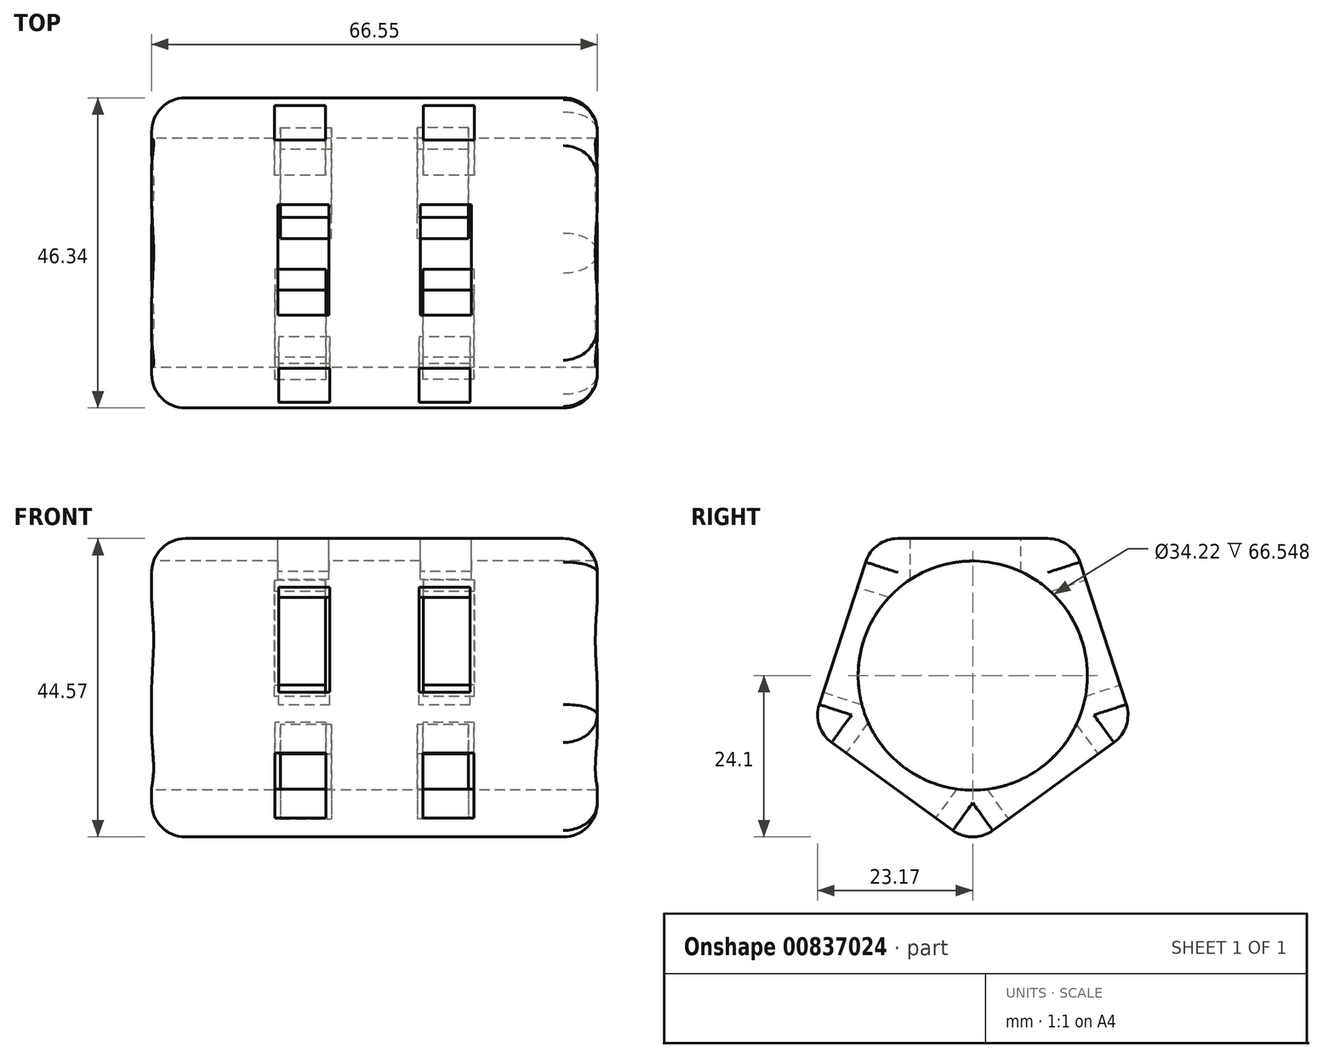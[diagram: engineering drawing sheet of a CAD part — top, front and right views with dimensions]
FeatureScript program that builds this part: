
annotation { "Feature Type Name" : "Feature", "Feature Type Description" : "" }
export const myFeature = defineFeature(function(context is Context, id is Id, definition is map)
    precondition{}
    {
        {
            var Q0;
            Q0=qCreatedBy(makeId("Right.planeOp"),FACE);
            var sketch = newSketch(context, id + "F0", { "sketchPlane" : qUnion([Q0])});
            skCircle(sketch, "E0.cCircle", {"center": v(0, 0) * mm, "radius": 20.47 * mm, "construction": true});
            skLineSegment(sketch, "E0.0", {"start": v(-14.87, 20.47) * mm, "end": v(14.87, 20.47) * mm});
            skLineSegment(sketch, "E0.1", {"start": v(14.87, 20.47) * mm, "end": v(24.07, -7.82) * mm});
            skLineSegment(sketch, "E0.2", {"start": v(24.07, -7.82) * mm, "end": v(0, -25.3) * mm});
            skLineSegment(sketch, "E0.3", {"start": v(0, -25.3) * mm, "end": v(-24.07, -7.82) * mm});
            skLineSegment(sketch, "E0.4", {"start": v(-24.07, -7.82) * mm, "end": v(-14.87, 20.47) * mm});
            skPoint(sketch, "E0.0.midPoint", {"position": v(0, 20.47) * mm});
            skCircle(sketch, "E1", {"center": v(0, 0) * mm, "radius": 17.1 * mm});
            skSolve(sketch);
        }
        {
            var Q0;
            Q0=makeQuery(id+"F0.imprint","IMPRINT",FACE,{"disambiguationData":[TD([[makeQuery(id+"F0.imprint","IMPRINT",EDGE,{"derivedFrom":sQuery(id+"F0.wireOp",EDGE,"E0.0")}),-1.0]])]});
            extrude(context, id + "F1", {"entities" : qUnion([Q0]), "depth" : 66.55 * mm, "offsetDistance" : 25.4 * mm});
        }
        {
            var Q0;
            Q0=makeQuery(id+"F1.opExtrude","CAP_EDGE",EDGE,{"disambiguationData":[OSD([sQuery(id+"F0.wireOp",EDGE,"E0.4")])],"isStart":false});
            var Q1;
            Q1=makeQuery(id+"F1.opExtrude","CAP_EDGE",EDGE,{"disambiguationData":[OSD([sQuery(id+"F0.wireOp",EDGE,"E0.0")])],"isStart":false});
            var Q2;
            Q2=makeQuery(id+"F1.opExtrude","CAP_EDGE",EDGE,{"disambiguationData":[OSD([sQuery(id+"F0.wireOp",EDGE,"E0.1")])],"isStart":false});
            var Q3;
            Q3=makeQuery(id+"F1.opExtrude","CAP_EDGE",EDGE,{"disambiguationData":[OSD([sQuery(id+"F0.wireOp",EDGE,"E0.2")])],"isStart":false});
            var Q4;
            Q4=makeQuery(id+"F1.opExtrude","CAP_EDGE",EDGE,{"disambiguationData":[OSD([sQuery(id+"F0.wireOp",EDGE,"E0.3")])],"isStart":false});
            fillet(context, id + "F2", {"entities" : qUnion([Q0, Q1, Q2, Q3, Q4]), "radius" : 5.08 * mm, "tangentPropagation" : true, "allowEdgeOverflow" : false});
        }
        {
            var Q0;
            Q0=makeQuery(id+"F1.opExtrude","CAP_EDGE",EDGE,{"disambiguationData":[OSD([sQuery(id+"F0.wireOp",EDGE,"E0.1")])],"isStart":true});
            var Q1;
            Q1=makeQuery(id+"F1.opExtrude","CAP_EDGE",EDGE,{"disambiguationData":[OSD([sQuery(id+"F0.wireOp",EDGE,"E0.0")])],"isStart":true});
            var Q2;
            Q2=makeQuery(id+"F1.opExtrude","CAP_EDGE",EDGE,{"disambiguationData":[OSD([sQuery(id+"F0.wireOp",EDGE,"E0.4")])],"isStart":true});
            var Q3;
            Q3=makeQuery(id+"F1.opExtrude","CAP_EDGE",EDGE,{"disambiguationData":[OSD([sQuery(id+"F0.wireOp",EDGE,"E0.3")])],"isStart":true});
            var Q4;
            Q4=makeQuery(id+"F1.opExtrude","CAP_EDGE",EDGE,{"disambiguationData":[OSD([sQuery(id+"F0.wireOp",EDGE,"E0.2")])],"isStart":true});
            var Q5;
            Q5=makeQuery(id+"F1.opExtrude","SWEPT_FACE",FACE,{"disambiguationData":[OSD([sQuery(id+"F0.wireOp",EDGE,"E0.4")])]});
            var Q6;
            Q6=makeQuery(id+"F1.opExtrude","SWEPT_FACE",FACE,{"disambiguationData":[OSD([sQuery(id+"F0.wireOp",EDGE,"E0.3")])]});
            var Q7;
            Q7=makeQuery(id+"F1.opExtrude","SWEPT_FACE",FACE,{"disambiguationData":[OSD([sQuery(id+"F0.wireOp",EDGE,"E0.2")])]});
            var Q8;
            Q8=makeQuery(id+"F1.opExtrude","SWEPT_FACE",FACE,{"disambiguationData":[OSD([sQuery(id+"F0.wireOp",EDGE,"E0.1")])]});
            fillet(context, id + "F3", {"entities" : qUnion([Q0, Q1, Q2, Q3, Q4, Q5, Q6, Q7, Q8]), "radius" : 5.08 * mm, "tangentPropagation" : true, "allowEdgeOverflow" : false});
        }
        {
            var Q0;
            Q0=makeQuery(id+"F1.opExtrude","SWEPT_FACE",FACE,{"disambiguationData":[OSD([sQuery(id+"F0.wireOp",EDGE,"E0.1")])]});
            var sketch = newSketch(context, id + "F4", { "sketchPlane" : qUnion([Q0])});
            skLineSegment(sketch, "E2", {"start": v(-33.27, 11.18) * mm, "end": v(-33.27, -11.18) * mm, "construction": true});
            skLineSegment(sketch, "E3", {"start": v(-5.08, 0) * mm, "end": v(-33.27, 0) * mm, "construction": true});
            skLineSegment(sketch, "E4", {"start": v(-33.27, 0) * mm, "end": v(-61.47, 0) * mm, "construction": true});
            skLineSegment(sketch, "E5.0.0", {"start": v(-61.47, 11.18) * mm, "end": v(-61.47, -11.18) * mm});
            skLineSegment(sketch, "E5.0.1", {"start": v(-61.47, -11.18) * mm, "end": v(-5.08, -11.18) * mm});
            skLineSegment(sketch, "E5.0.2", {"start": v(-5.08, -11.18) * mm, "end": v(-5.08, 11.18) * mm});
            skLineSegment(sketch, "E5.0.3", {"start": v(-5.08, 11.18) * mm, "end": v(-61.47, 11.18) * mm});
            skLineSegment(sketch, "E6.bottom", {"start": v(-48.2, 8.37) * mm, "end": v(-40.59, 8.37) * mm, "construction": true});
            skLineSegment(sketch, "E6.top", {"start": v(-48.2, -8.14) * mm, "end": v(-40.59, -8.14) * mm, "construction": true});
            skLineSegment(sketch, "E6.left", {"start": v(-48.2, 8.37) * mm, "end": v(-48.2, -8.14) * mm, "construction": true});
            skLineSegment(sketch, "E6.right", {"start": v(-40.59, 8.37) * mm, "end": v(-40.59, -8.14) * mm, "construction": true});
            skLineSegment(sketch, "E7.MirrorCS", {"start": v(-18.34, 8.37) * mm, "end": v(-18.34, -8.14) * mm});
            skLineSegment(sketch, "E8.MirrorCS", {"start": v(-18.34, 8.37) * mm, "end": v(-25.96, 8.37) * mm});
            skLineSegment(sketch, "E9.MirrorCS", {"start": v(-25.96, 8.37) * mm, "end": v(-25.96, -8.14) * mm});
            skLineSegment(sketch, "E10.MirrorCS", {"start": v(-18.34, -8.14) * mm, "end": v(-25.96, -8.14) * mm});
            skLineSegment(sketch, "E11.MirrorCS", {"start": v(-48.2, 8.37) * mm, "end": v(-40.59, 8.37) * mm});
            skLineSegment(sketch, "E12.MirrorCS", {"start": v(-48.2, -8.14) * mm, "end": v(-40.59, -8.14) * mm});
            skLineSegment(sketch, "E13.MirrorCS", {"start": v(-48.2, 8.37) * mm, "end": v(-48.2, -8.14) * mm});
            skLineSegment(sketch, "E14.MirrorCS", {"start": v(-40.59, 8.37) * mm, "end": v(-40.59, -8.14) * mm});
            skSolve(sketch);
        }
        {
            var Q0;
            Q0=makeQuery(id+"F4.imprint","IMPRINT",FACE,{"disambiguationData":[TD([[makeQuery(id+"F4.imprint","IMPRINT",EDGE,{"derivedFrom":sQuery(id+"F4.wireOp",EDGE,"E11.MirrorCS")}),-1.0]])]});
            var Q1;
            Q1=makeQuery(id+"F4.imprint","IMPRINT",FACE,{"disambiguationData":[TD([[makeQuery(id+"F4.imprint","IMPRINT",EDGE,{"derivedFrom":sQuery(id+"F4.wireOp",EDGE,"E7.MirrorCS")}),-1.0]])]});
            extrude(context, id + "F5", {"entities" : qUnion([Q0, Q1]), "operationType" : NewBodyOperationType.REMOVE, "oppositeDirection" : true, "depth" : 7.87 * mm, "offsetDistance" : 25.4 * mm});
        }
        {
            var Q0;
            Q0=makeQuery(id+"F1.opExtrude","SWEPT_FACE",FACE,{"disambiguationData":[OSD([sQuery(id+"F0.wireOp",EDGE,"E0.2")])]});
            var sketch = newSketch(context, id + "F6", { "sketchPlane" : qUnion([Q0])});
            skLineSegment(sketch, "E15", {"start": v(33.27, -11.18) * mm, "end": v(33.27, 11.18) * mm, "construction": true});
            skLineSegment(sketch, "E16", {"start": v(5.08, 0) * mm, "end": v(61.47, 0) * mm, "construction": true});
            skLineSegment(sketch, "E17.bottom", {"start": v(47.33, -8.23) * mm, "end": v(39.7, -8.23) * mm});
            skLineSegment(sketch, "E17.top", {"start": v(47.33, 8.28) * mm, "end": v(39.7, 8.28) * mm});
            skLineSegment(sketch, "E17.left", {"start": v(47.33, -8.23) * mm, "end": v(47.33, 8.28) * mm});
            skLineSegment(sketch, "E17.right", {"start": v(39.7, -8.23) * mm, "end": v(39.7, 8.28) * mm});
            skLineSegment(sketch, "E18.MirrorCS", {"start": v(19.22, -8.23) * mm, "end": v(19.22, 8.28) * mm});
            skLineSegment(sketch, "E19.MirrorCS", {"start": v(26.84, -8.23) * mm, "end": v(26.84, 8.28) * mm});
            skLineSegment(sketch, "E20.MirrorCS", {"start": v(19.22, -8.23) * mm, "end": v(26.84, -8.23) * mm});
            skLineSegment(sketch, "E21.MirrorCS", {"start": v(19.22, 8.28) * mm, "end": v(26.84, 8.28) * mm});
            skSolve(sketch);
        }
        {
            var Q0;
            Q0=makeQuery(id+"F6.imprint","IMPRINT",FACE,{"disambiguationData":[TD([[makeQuery(id+"F6.imprint","IMPRINT",EDGE,{"derivedFrom":sQuery(id+"F6.wireOp",EDGE,"E18.MirrorCS")}),-1.0]])]});
            var Q1;
            Q1=makeQuery(id+"F6.imprint","IMPRINT",FACE,{"disambiguationData":[TD([[makeQuery(id+"F6.imprint","IMPRINT",EDGE,{"derivedFrom":sQuery(id+"F6.wireOp",EDGE,"E17.bottom")}),-1.0]])]});
            extrude(context, id + "F7", {"entities" : qUnion([Q0, Q1]), "operationType" : NewBodyOperationType.REMOVE, "oppositeDirection" : true, "depth" : 7.11 * mm, "offsetDistance" : 25.4 * mm});
        }
        {
            var Q0;
            Q0=makeQuery(id+"F1.opExtrude","SWEPT_FACE",FACE,{"disambiguationData":[OSD([sQuery(id+"F0.wireOp",EDGE,"E0.0")])]});
            var sketch = newSketch(context, id + "F8", { "sketchPlane" : qUnion([Q0])});
            skLineSegment(sketch, "E22", {"start": v(33.27, 11.18) * mm, "end": v(33.27, -11.18) * mm, "construction": true});
            skLineSegment(sketch, "E23", {"start": v(61.47, 0) * mm, "end": v(5.08, 0) * mm, "construction": true});
            skLineSegment(sketch, "E24.bottom", {"start": v(18.83, 7.2) * mm, "end": v(26.45, 7.2) * mm});
            skLineSegment(sketch, "E24.top", {"start": v(18.83, -9.3) * mm, "end": v(26.45, -9.3) * mm});
            skLineSegment(sketch, "E24.left", {"start": v(18.83, 7.2) * mm, "end": v(18.83, -9.3) * mm});
            skLineSegment(sketch, "E24.right", {"start": v(26.45, 7.2) * mm, "end": v(26.45, -9.3) * mm});
            skLineSegment(sketch, "E25.MirrorCS", {"start": v(47.71, 7.2) * mm, "end": v(47.71, -9.3) * mm});
            skLineSegment(sketch, "E26.MirrorCS", {"start": v(40.1, 7.2) * mm, "end": v(40.1, -9.3) * mm});
            skLineSegment(sketch, "E27.MirrorCS", {"start": v(47.71, 7.2) * mm, "end": v(40.1, 7.2) * mm});
            skLineSegment(sketch, "E28.MirrorCS", {"start": v(47.71, -9.3) * mm, "end": v(40.1, -9.3) * mm});
            skSolve(sketch);
        }
        {
            var Q0;
            Q0 = qSketchRegion(id + "F8", true);
            extrude(context, id + "F9", {"entities" : qUnion([Q0]), "operationType" : NewBodyOperationType.REMOVE, "oppositeDirection" : true, "depth" : 12.2 * mm, "offsetDistance" : 25.4 * mm});
        }
        {
            var Q0;
            Q0=makeQuery(id+"F1.opExtrude","SWEPT_FACE",FACE,{"disambiguationData":[OSD([sQuery(id+"F0.wireOp",EDGE,"E0.4")])]});
            var sketch = newSketch(context, id + "F10", { "sketchPlane" : qUnion([Q0])});
            skLineSegment(sketch, "E29", {"start": v(33.27, 11.18) * mm, "end": v(33.27, -11.18) * mm, "construction": true});
            skLineSegment(sketch, "E30", {"start": v(61.47, 0) * mm, "end": v(5.08, 0) * mm, "construction": true});
            skLineSegment(sketch, "E31.bottom", {"start": v(19, 7.22) * mm, "end": v(26.62, 7.22) * mm});
            skLineSegment(sketch, "E31.top", {"start": v(19, -9.3) * mm, "end": v(26.62, -9.3) * mm});
            skLineSegment(sketch, "E31.left", {"start": v(19, 7.22) * mm, "end": v(19, -9.3) * mm});
            skLineSegment(sketch, "E31.right", {"start": v(26.62, 7.22) * mm, "end": v(26.62, -9.3) * mm});
            skLineSegment(sketch, "E32.MirrorCS", {"start": v(47.54, -9.3) * mm, "end": v(39.92, -9.3) * mm});
            skLineSegment(sketch, "E33.MirrorCS", {"start": v(47.54, 7.22) * mm, "end": v(47.54, -9.3) * mm});
            skLineSegment(sketch, "E34.MirrorCS", {"start": v(47.54, 7.22) * mm, "end": v(39.92, 7.22) * mm});
            skLineSegment(sketch, "E35.MirrorCS", {"start": v(39.92, 7.22) * mm, "end": v(39.92, -9.3) * mm});
            skSolve(sketch);
        }
        {
            var Q0;
            Q0 = qSketchRegion(id + "F10", true);
            extrude(context, id + "F11", {"entities" : qUnion([Q0]), "operationType" : NewBodyOperationType.REMOVE, "oppositeDirection" : true, "depth" : 24.38 * mm, "offsetDistance" : 25.4 * mm});
        }
        {
            var Q0;
            Q0=makeQuery(id+"F1.opExtrude","SWEPT_FACE",FACE,{"disambiguationData":[OSD([sQuery(id+"F0.wireOp",EDGE,"E0.3")])]});
            var sketch = newSketch(context, id + "F12", { "sketchPlane" : qUnion([Q0])});
            skLineSegment(sketch, "E36", {"start": v(33.27, 11.18) * mm, "end": v(33.27, -11.18) * mm, "construction": true});
            skLineSegment(sketch, "E37", {"start": v(61.47, 0) * mm, "end": v(5.08, 0) * mm, "construction": true});
            skLineSegment(sketch, "E38.bottom", {"start": v(18.4, 8.5) * mm, "end": v(26.01, 8.5) * mm});
            skLineSegment(sketch, "E38.top", {"start": v(18.4, -8) * mm, "end": v(26.01, -8) * mm});
            skLineSegment(sketch, "E38.left", {"start": v(18.4, 8.5) * mm, "end": v(18.4, -8) * mm});
            skLineSegment(sketch, "E38.right", {"start": v(26.01, 8.5) * mm, "end": v(26.01, -8) * mm});
            skLineSegment(sketch, "E39.MirrorCS", {"start": v(40.54, 8.5) * mm, "end": v(40.54, -8) * mm});
            skLineSegment(sketch, "E40.MirrorCS", {"start": v(48.16, -8) * mm, "end": v(40.54, -8) * mm});
            skLineSegment(sketch, "E41.MirrorCS", {"start": v(48.16, 8.5) * mm, "end": v(40.54, 8.5) * mm});
            skLineSegment(sketch, "E42.MirrorCS", {"start": v(48.16, 8.5) * mm, "end": v(48.16, -8) * mm});
            skSolve(sketch);
        }
        {
            var Q0;
            Q0=makeQuery(id+"F12.imprint","IMPRINT",FACE,{"disambiguationData":[TD([[makeQuery(id+"F12.imprint","IMPRINT",EDGE,{"derivedFrom":sQuery(id+"F12.wireOp",EDGE,"E38.bottom")}),-1.0]])]});
            var Q1;
            Q1=makeQuery(id+"F12.imprint","IMPRINT",FACE,{"disambiguationData":[TD([[makeQuery(id+"F12.imprint","IMPRINT",EDGE,{"derivedFrom":sQuery(id+"F12.wireOp",EDGE,"E39.MirrorCS")}),1.0]])]});
            extrude(context, id + "F13", {"entities" : qUnion([Q0, Q1]), "operationType" : NewBodyOperationType.REMOVE, "oppositeDirection" : true, "depth" : 25.4 * mm, "offsetDistance" : 25.4 * mm});
        }
    });
